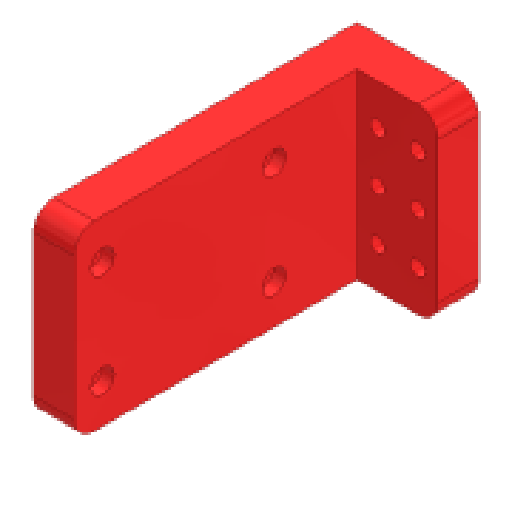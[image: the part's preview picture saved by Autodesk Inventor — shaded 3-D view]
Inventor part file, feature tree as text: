
AUTODESK INVENTOR PART (.ipt)
format: ipt  version: 2024.3 (Build 283343000, 343)  size: 153,600 bytes
history: native  units: mm
features: sketch x5, hole x3, extrude x2, fillet x1
ambient origin geometry x8: Origin, YZ Plane, XZ Plane, XY Plane, X Axis, Y Axis, Z Axis, Center Point
bodies: Solid1 (feature_tree)
feature tree (11):
  extrude  "Extrusion1"  Depth=45.0mm
  hole  "Hole1"  [1 undecoded]
  extrude  "Extrusion2"  Depth=10.0mm
  hole  "Hole2"  [1 undecoded]
  hole  "Hole3"  [1 undecoded]
  fillet  "Fillet1"  Radius=25.5mm
  sketch  "Sketch1"  dims[d0=20.0mm d1=45.0mm]
  sketch  "Sketch2"  dims[d2=10.0mm d3=10.0mm d4=0.0mm]
  sketch  "Sketch3"  dims[d5=10.0mm d6=25.0mm]
  sketch  "Sketch4"  dims[d7=3.6mm d8=6.0mm d9=6.3mm d10=2.0mm d11=90.0deg d12=3.0mm d13=0.0mm d14=10.0mm]
  sketch  "Sketch5"  dims[d15=80.0mm d16=0.0mm d17=42.5mm d18=25.5mm d19=7.0mm d20=3.0mm d21=6.0mm d22=5.5mm d23=2.0mm d24=90.0deg d25=8.0mm d26=0.0mm d27=5.8mm d28=6.0mm d29=4.0mm d30=2.0mm d31=90.0deg d32=3.0mm d33=0.0mm d34=5.0mm]
note: 3 required parameter values undecoded (feature->parameter linkage not recoverable at this tier; creation-order binding heuristic only, values carry confidence <= 0.55)
